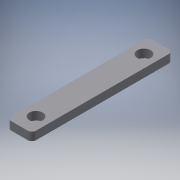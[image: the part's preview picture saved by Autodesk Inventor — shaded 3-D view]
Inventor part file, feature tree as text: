
AUTODESK INVENTOR PART (.ipt)
format: ipt  version: 2018 (Build 220112000, 112)  size: 114,688 bytes
history: native  units: mm
features: reference x3, other x3, extrude x1, fillet x1, sketch x1
ambient origin geometry x8: Origin, YZ Plane, XZ Plane, XY Plane, X Axis, Y Axis, Z Axis, Center Point
bodies: Solid1 (feature_tree)
feature tree (9):
  extrude  "Extrusion1"  Depth=1.0mm
  fillet  "Fillet1"  Radius=4.0mm
  sketch  "Sketch1"  dims[d0=4.0mm d1=3.0mm d2=4.0mm d3=6.0mm d4=3.25mm d5=3.25mm d6=2.0mm d7=0.0mm d8=1.0mm]
  reference  "Reference1"
  reference  "Reference2"
  reference  "Reference3"
  other  "Glyptodon.iam"
  other  "SyringeTailLeverAttachment:1"
  other  "Tail3:1"
